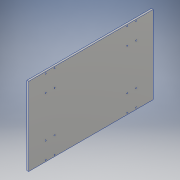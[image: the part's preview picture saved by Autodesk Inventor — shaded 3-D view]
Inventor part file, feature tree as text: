
AUTODESK INVENTOR PART (.ipt)
format: ipt  version: 2017 (Build 210142000, 142)  size: 142,848 bytes
history: native  units: in
note: dims shown in document units (in); Inventor stores cm internally (conversion verified against a paired STEP export)
features: extrude x1, sketch x1
ambient origin geometry x8: Origin, YZ Plane, XZ Plane, XY Plane, X Axis, Y Axis, Z Axis, Center Point
bodies: Solid1 (feature_tree)
feature tree (2):
  extrude  "Extrusion1"  Depth=17.5in
  sketch  "Sketch1"  dims[d0=11.0in d1=17.5in d2=0.153in d3=0.153in d4=1.26in d5=0.236in d6=0.236in d7=2.37in d8=0.153in d9=0.153in d10=2.364in d11=2.364in d12=2.37in d13=0.153in d14=0.153in d15=0.153in d16=0.153in d17=2.37in d18=2.37in d19=0.236in d20=0.236in d22=2.364in d23=2.364in d24=1.26in d25=0.153in d26=0.153in d27=0.236in d28=0.236in d29=0.153in d30=0.153in d32=1.26in d33=1.26in d34=2.37in d35=2.37in d36=0.153in d37=0.153in d38=0.153in d39=0.153in d40=0.25in d41=0.0in]
